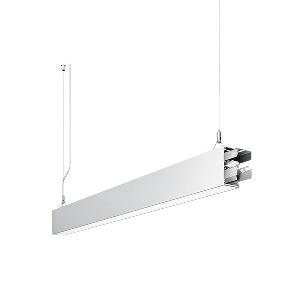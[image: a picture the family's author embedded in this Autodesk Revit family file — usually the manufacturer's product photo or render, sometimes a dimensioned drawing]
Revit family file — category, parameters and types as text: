
# Revit family: idoo_line_-_ilp_4000_830_d_sta_00805736_b481
name_source: partatom
category: Lighting Fixtures
units: mm (PartAtom-declared; Revit-internal decimal feet)

## family parameters
Cut with Voids When Loaded = No
Host = Face
Light Source = No
Part Type = Normal
Room Calculation Point = No
Round Connector Dimension = Use Diameter
Shared = No

## types (1)
- IDOO.line - ILP 4000/830/D STA (1 x LED, 3750 lm, 3000K)
    Apparent Load = 29 VA
    Approval mark = CE
    CIE Flux Codes = 66 91 98 40 100
    Color Rendering = 80-89
    Color Temperature = 3000K
    Control Gear = Electronic ballast
    Default Elevation = 1800 mm
    Description = ILP 4000/830/D|Suspended luminaire|light source: LED|connected load: 220-240 V, 50/60 Hz|Power consumption: approx. 29 W|standby: approx. 0,15|luminous flux: 3750 lm|luminous efficacy: 129 lm/W|light distribution: Direct/indirect|direct ratio: approx. 40 %|colour temperature: Warm white, ca. 3000 K|color rendering index (CRI): >= 80|chromaticity tolerance:  3 SDCM|System of protection: IP 40|technology: Continuously dimmable|luminaire body|material: Sectional aluminium|colour: White|lamp cover: Acrylic (PMMA), Clear|mains lead: 2.00 m With free stranded wires|Fastening: Steel cable 0.3 - 0.7 m|glare control: Prism aperture|luminance(L65): <= 2700 cd/m|unified glare rating(4H 8H): <=  16|special features: DALI Load 1x, TouchDIM - dimming via standard switch, Through-wired, up to 18 m on one mains connection, Flicker-free, Suitable as emergency lighting, Start luminaire with mains connection, Mechanical and electrical connection of the individual modules without tools|
    Frequency = 50 Hz
    Height = 110 mm
    Lamp = 1 x LED
    Lamp Light Flux = 3750 lm
    Lamp count = 1
    Length = 1408 mm
    Luminous efficacy = 129 lm/W
    Manufacturer = Waldmann
    ModVariant = No
    Model = 00805736
    Mounting Place = Ceiling
    Mounting Type = Pendant
    Number of Poles = 1
    OnlyDefault = Yes
    Power Factor = 1
    Product Name = IDOO.line - ILP 4000/830/D STA
    Product group = Suspended luminaire
    ProductGroupID = 9
    Protection Class = Protection class I
    Protection Degree = IP 40
    RLX_Detail_Level = 1
    RLX_Emergency_Light_Flux = 0 lm
    RLX_Emergency_Type = 0
    RLX_Emergency_Type_DB = No
    RlxData = <blob elided: 21981 chars, md5=a7bc139b>
    Socket = socket
    Standby Power = 0 W
    System Light Flux = 3750 lm
    System Power = 29 W
    Type Comments = Product without accessories
    Type Image = 113307000-00692585.jpg
    URL = http://relux.com
    VarID = ---
    Voltage = 230 V
    Voltage Range = 220-240 V
    Weight = 0.00 kg
    Width = 60 mm  [stored 0.19685 ft]

note: [stored X ft] marks values corroborated as IEEE doubles in the binary element streams (Revit-internal decimal feet)

## geometry (parser evidence)
native form markers: Blend x4, Sweep x14
no freeform markers — native parametric forms only
